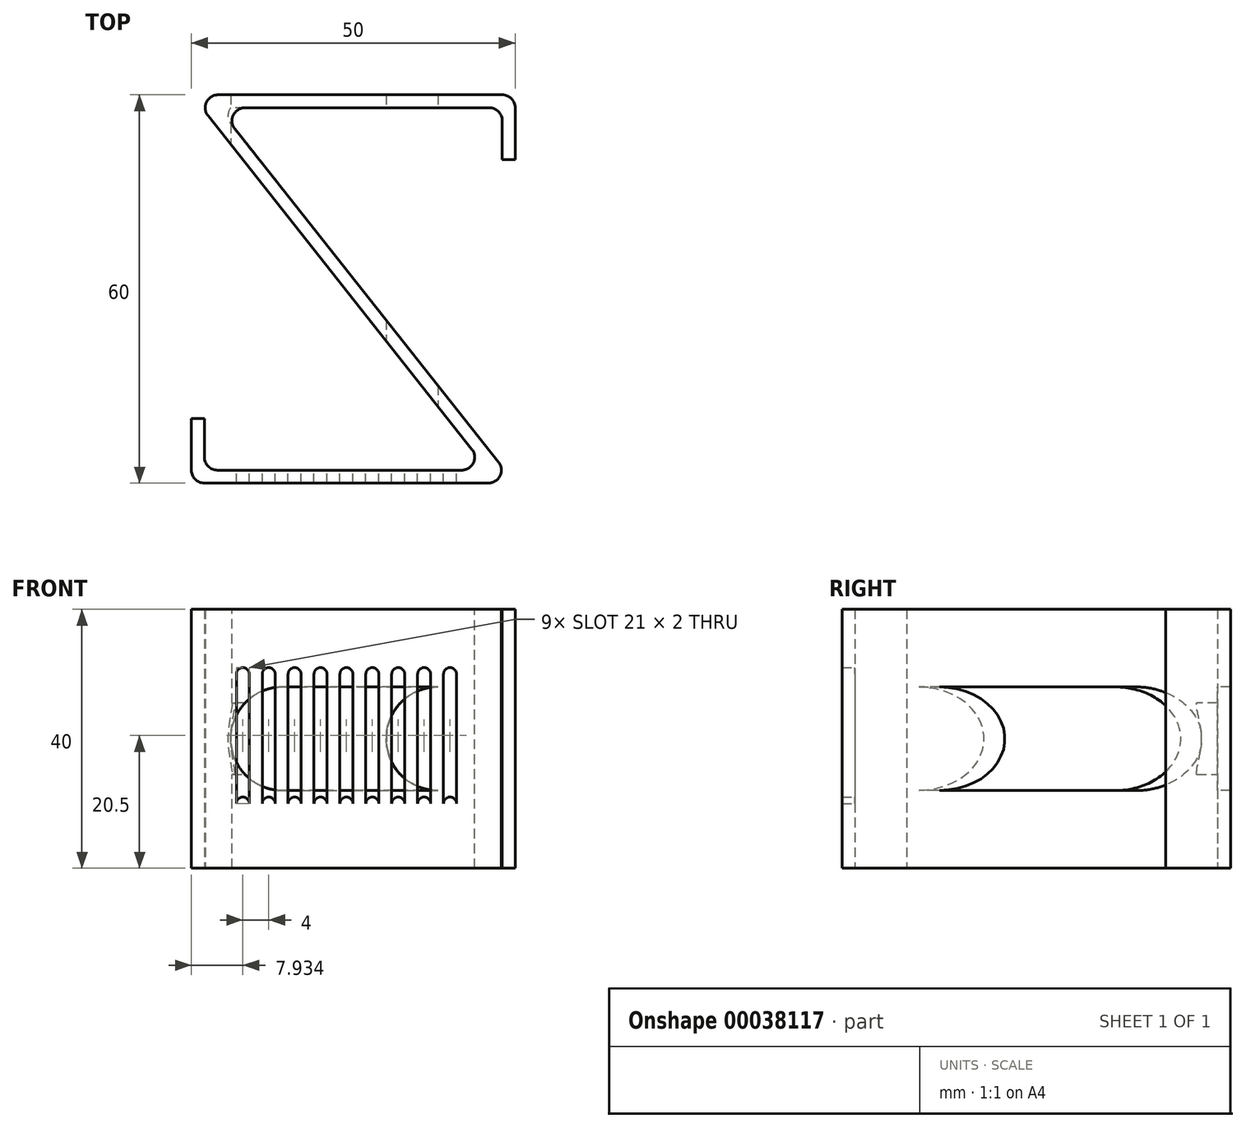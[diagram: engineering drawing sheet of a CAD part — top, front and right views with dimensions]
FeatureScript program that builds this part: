
annotation { "Feature Type Name" : "Feature", "Feature Type Description" : "" }
export const myFeature = defineFeature(function(context is Context, id is Id, definition is map)
    precondition{}
    {
        {
            assignVariable(context, id + "F0", {"name" : "WallThickness", "anyValue" : 2});
        }
        {
            assignVariable(context, id + "F1", {"name" : "Height", "anyValue" : 60});
        }
        {
            var Q0;
            Q0=qCreatedBy(makeId("Top.planeOp"),FACE);
            var sketch = newSketch(context, id + "F2", { "sketchPlane" : qUnion([Q0])});
            skLineSegment(sketch, "E0", {"start": v(0, 10) * mm, "end": v(0, 0) * mm});
            skLineSegment(sketch, "E1", {"start": v(0, 0) * mm, "end": v(50, 0) * mm});
            skLineSegment(sketch, "E2", {"start": v(50, 0) * mm, "end": v(4.13, 58) * mm});
            skLineSegment(sketch, "E3", {"start": v(4.13, 58) * mm, "end": v(48, 58) * mm});
            skLineSegment(sketch, "E4", {"start": v(48, 58) * mm, "end": v(48, 50) * mm});
            skLineSegment(sketch, "E5", {"start": v(48, 50) * mm, "end": v(50, 50) * mm});
            skLineSegment(sketch, "E6", {"start": v(50, 50) * mm, "end": v(50, 60) * mm});
            skLineSegment(sketch, "E7", {"start": v(50, 60) * mm, "end": v(0, 60) * mm});
            skLineSegment(sketch, "E8", {"start": v(0, 60) * mm, "end": v(45.87, 2) * mm});
            skLineSegment(sketch, "E9", {"start": v(45.87, 2) * mm, "end": v(2, 2) * mm});
            skLineSegment(sketch, "E10", {"start": v(2, 2) * mm, "end": v(2, 10) * mm});
            skLineSegment(sketch, "E11", {"start": v(2, 10) * mm, "end": v(0, 10) * mm});
            skSolve(sketch);
        }
        {
            assignVariable(context, id + "F3", {"name" : "Width", "anyValue" : 40});
        }
        {
            var Q0;
            Q0=makeQuery(id+"F2.imprint","IMPRINT",FACE,{"disambiguationData":[TD([[makeQuery(id+"F2.imprint","IMPRINT",EDGE,{"derivedFrom":sQuery(id+"F2.wireOp",EDGE,"E0")}),1.0]])]});
            extrude(context, id + "F4", {"entities" : qUnion([Q0]), "depth" : (getVariable(context, 'Width')) * mm});
        }
        {
            var Q0;
            Q0=makeQuery(id+"F4.opExtrude","SWEPT_FACE",FACE,{"disambiguationData":[OSD([sQuery(id+"F2.wireOp",EDGE,"E3")])]});
            var sketch = newSketch(context, id + "F5", { "sketchPlane" : qUnion([Q0])});
            skLineSegment(sketch, "E12.1", {"start": v(4.13, 40) * mm, "end": v(48, 40) * mm});
            skLineSegment(sketch, "E12.2", {"start": v(48, 40) * mm, "end": v(48, 0) * mm});
            skLineSegment(sketch, "E12.3", {"start": v(4.13, 0) * mm, "end": v(48, 0) * mm});
            skLineSegment(sketch, "E12.4", {"start": v(4.13, 40) * mm, "end": v(4.13, 0) * mm});
            skLineSegment(sketch, "E13", {"start": v(26.07, 40) * mm, "end": v(26.07, 0) * mm, "construction": true});
            skCircle(sketch, "E14", {"center": v(14.07, 20) * mm, "radius": 8 * mm});
            skPoint(sketch, "E14.centerSnap0", {"position": v(26.07, 20) * mm});
            skCircle(sketch, "E15.MirrorC", {"center": v(38.07, 20) * mm, "radius": 8 * mm});
            skLineSegment(sketch, "E16", {"start": v(14.07, 28) * mm, "end": v(38.07, 28) * mm});
            skLineSegment(sketch, "E17", {"start": v(38.07, 12) * mm, "end": v(14.07, 12) * mm});
            skSolve(sketch);
        }
        {
            var Q0;
            {var subQ0=sQuery(id+"F5.wireOp",EDGE,"E14");var subQ2=makeQuery(id+"F5.imprint","INTERSECT",VERTEX,{"derivedFrom":[subQ0,sQuery(id+"F5.wireOp",EDGE,"E16")]});Q0=makeQuery(id+"F5.imprint","IMPRINT",FACE,{"disambiguationData":[TD([[makeQuery(id+"F5.imprint","IMPRINT",EDGE,{"disambiguationData":[TD([[subQ2,-1.0]])],"derivedFrom":subQ0}),1.0]])]});}
            var Q1;
            {var subQ1=sQuery(id+"F5.wireOp",EDGE,"E16");Q1=makeQuery(id+"F5.imprint","IMPRINT",FACE,{"disambiguationData":[TD([[makeQuery(id+"F5.imprint","IMPRINT",EDGE,{"derivedFrom":subQ1}),-1.0]])]});}
            var Q2;
            {var subQ0=sQuery(id+"F5.wireOp",EDGE,"E15.MirrorC");var subQ2=makeQuery(id+"F5.imprint","INTERSECT",VERTEX,{"derivedFrom":[subQ0,sQuery(id+"F5.wireOp",EDGE,"E16")]});Q2=makeQuery(id+"F5.imprint","IMPRINT",FACE,{"disambiguationData":[TD([[makeQuery(id+"F5.imprint","IMPRINT",EDGE,{"disambiguationData":[TD([[subQ2,-1.0]])],"derivedFrom":subQ0}),-1.0]])]});}
            extrude(context, id + "F6", {"entities" : qUnion([Q0, Q1, Q2]), "operationType" : NewBodyOperationType.REMOVE, "endBound" : BoundingType.THROUGH_ALL, "oppositeDirection" : true, "depth" : 25 * mm, "hasSecondDirection" : true, "secondDirectionOppositeDirection" : false, "secondDirectionDepth" : (getVariable(context, 'Height') - (getVariable(context, 'WallThickness') * 2)) * mm});
        }
        {
            var Q0;
            Q0=makeQuery(id+"F4.opExtrude","SWEPT_FACE",FACE,{"disambiguationData":[OSD([sQuery(id+"F2.wireOp",EDGE,"E9")])]});
            var sketch = newSketch(context, id + "F7", { "sketchPlane" : qUnion([Q0])});
            skLineSegment(sketch, "E18.0", {"start": v(-45.87, 0) * mm, "end": v(-2, 0) * mm});
            skLineSegment(sketch, "E18.1", {"start": v(-2, 40) * mm, "end": v(-2, 0) * mm});
            skLineSegment(sketch, "E18.2", {"start": v(-45.87, 40) * mm, "end": v(-2, 40) * mm});
            skLineSegment(sketch, "E18.3", {"start": v(-45.87, 40) * mm, "end": v(-45.87, 0) * mm});
            skLineSegment(sketch, "E19", {"start": v(-23.93, 40) * mm, "end": v(-23.93, 0) * mm, "construction": true});
            skCircle(sketch, "E20", {"center": v(-23.93, 30) * mm, "radius": 1 * mm});
            skLineSegment(sketch, "E21", {"start": v(-45.87, 20) * mm, "end": v(-2, 20) * mm, "construction": true});
            skCircle(sketch, "E22.MirrorC", {"center": v(-23.93, 10) * mm, "radius": 1 * mm});
            skLineSegment(sketch, "E23", {"start": v(-22.93, 10) * mm, "end": v(-22.93, 30) * mm});
            skLineSegment(sketch, "E24", {"start": v(-24.93, 30) * mm, "end": v(-24.93, 10) * mm});
            skCircle(sketch, "E25.1.0.0", {"center": v(-19.93, 10) * mm, "radius": 1 * mm});
            skCircle(sketch, "E25.1.0.1", {"center": v(-19.93, 30) * mm, "radius": 1 * mm});
            skLineSegment(sketch, "E25.1.0.2", {"start": v(-20.93, 30) * mm, "end": v(-20.93, 10) * mm});
            skLineSegment(sketch, "E25.1.0.3", {"start": v(-18.93, 10) * mm, "end": v(-18.93, 30) * mm});
            skCircle(sketch, "E25.2.0.0", {"center": v(-15.93, 10) * mm, "radius": 1 * mm});
            skCircle(sketch, "E25.2.0.1", {"center": v(-15.93, 30) * mm, "radius": 1 * mm});
            skLineSegment(sketch, "E25.2.0.2", {"start": v(-16.93, 30) * mm, "end": v(-16.93, 10) * mm});
            skLineSegment(sketch, "E25.2.0.3", {"start": v(-14.93, 10) * mm, "end": v(-14.93, 30) * mm});
            skCircle(sketch, "E25.3.0.0", {"center": v(-11.93, 10) * mm, "radius": 1 * mm});
            skCircle(sketch, "E25.3.0.1", {"center": v(-11.93, 30) * mm, "radius": 1 * mm});
            skLineSegment(sketch, "E25.3.0.2", {"start": v(-12.93, 30) * mm, "end": v(-12.93, 10) * mm});
            skLineSegment(sketch, "E25.3.0.3", {"start": v(-10.93, 10) * mm, "end": v(-10.93, 30) * mm});
            skCircle(sketch, "E25.4.0.0", {"center": v(-7.93, 10) * mm, "radius": 1 * mm});
            skCircle(sketch, "E25.4.0.1", {"center": v(-7.93, 30) * mm, "radius": 1 * mm});
            skLineSegment(sketch, "E25.4.0.2", {"start": v(-8.93, 30) * mm, "end": v(-8.93, 10) * mm});
            skLineSegment(sketch, "E25.4.0.3", {"start": v(-6.93, 10) * mm, "end": v(-6.93, 30) * mm});
            skLineSegment(sketch, "E25.direction1", {"start": v(-23.93, 10) * mm, "end": v(-19.93, 10) * mm, "construction": true});
            skLineSegment(sketch, "E26.1.0.0", {"start": v(-28.93, 30) * mm, "end": v(-28.93, 10) * mm});
            skLineSegment(sketch, "E26.1.0.1", {"start": v(-26.93, 10) * mm, "end": v(-26.93, 30) * mm});
            skCircle(sketch, "E26.1.0.2", {"center": v(-27.93, 10) * mm, "radius": 1 * mm});
            skCircle(sketch, "E26.1.0.3", {"center": v(-27.93, 30) * mm, "radius": 1 * mm});
            skLineSegment(sketch, "E26.2.0.0", {"start": v(-32.93, 30) * mm, "end": v(-32.93, 10) * mm});
            skLineSegment(sketch, "E26.2.0.1", {"start": v(-30.93, 10) * mm, "end": v(-30.93, 30) * mm});
            skCircle(sketch, "E26.2.0.2", {"center": v(-31.93, 10) * mm, "radius": 1 * mm});
            skCircle(sketch, "E26.2.0.3", {"center": v(-31.93, 30) * mm, "radius": 1 * mm});
            skLineSegment(sketch, "E26.3.0.0", {"start": v(-36.93, 30) * mm, "end": v(-36.93, 10) * mm});
            skLineSegment(sketch, "E26.3.0.1", {"start": v(-34.93, 10) * mm, "end": v(-34.93, 30) * mm});
            skCircle(sketch, "E26.3.0.2", {"center": v(-35.93, 10) * mm, "radius": 1 * mm});
            skCircle(sketch, "E26.3.0.3", {"center": v(-35.93, 30) * mm, "radius": 1 * mm});
            skLineSegment(sketch, "E26.4.0.0", {"start": v(-40.93, 30) * mm, "end": v(-40.93, 10) * mm});
            skLineSegment(sketch, "E26.4.0.1", {"start": v(-38.93, 10) * mm, "end": v(-38.93, 30) * mm});
            skCircle(sketch, "E26.4.0.2", {"center": v(-39.93, 10) * mm, "radius": 1 * mm});
            skCircle(sketch, "E26.4.0.3", {"center": v(-39.93, 30) * mm, "radius": 1 * mm});
            skLineSegment(sketch, "E26.direction1", {"start": v(-24.93, 10) * mm, "end": v(-28.93, 10) * mm, "construction": true});
            skSolve(sketch);
        }
        {
            var Q0;
            {var subQ0=sQuery(id+"F7.wireOp",EDGE,"E25.4.0.0");var subQ2=makeQuery(id+"F7.imprint","INTERSECT",VERTEX,{"derivedFrom":[subQ0,sQuery(id+"F7.wireOp",EDGE,"E25.4.0.2")]});Q0=makeQuery(id+"F7.imprint","IMPRINT",FACE,{"disambiguationData":[TD([[makeQuery(id+"F7.imprint","IMPRINT",EDGE,{"disambiguationData":[TD([[subQ2,1.0]])],"derivedFrom":subQ0}),-1.0]])]});}
            var Q1;
            {var subQ2=sQuery(id+"F7.wireOp",EDGE,"E25.4.0.2");Q1=makeQuery(id+"F7.imprint","IMPRINT",FACE,{"disambiguationData":[TD([[makeQuery(id+"F7.imprint","IMPRINT",EDGE,{"derivedFrom":subQ2}),1.0]])]});}
            var Q2;
            {var subQ0=sQuery(id+"F7.wireOp",EDGE,"E25.4.0.1");var subQ2=makeQuery(id+"F7.imprint","INTERSECT",VERTEX,{"derivedFrom":[subQ0,sQuery(id+"F7.wireOp",EDGE,"E25.4.0.2")]});Q2=makeQuery(id+"F7.imprint","IMPRINT",FACE,{"disambiguationData":[TD([[makeQuery(id+"F7.imprint","IMPRINT",EDGE,{"disambiguationData":[TD([[subQ2,1.0]])],"derivedFrom":subQ0}),1.0]])]});}
            var Q3;
            {var subQ0=sQuery(id+"F7.wireOp",EDGE,"E25.3.0.0");var subQ2=makeQuery(id+"F7.imprint","INTERSECT",VERTEX,{"derivedFrom":[subQ0,sQuery(id+"F7.wireOp",EDGE,"E25.3.0.2")]});Q3=makeQuery(id+"F7.imprint","IMPRINT",FACE,{"disambiguationData":[TD([[makeQuery(id+"F7.imprint","IMPRINT",EDGE,{"disambiguationData":[TD([[subQ2,1.0]])],"derivedFrom":subQ0}),-1.0]])]});}
            var Q4;
            {var subQ0=sQuery(id+"F7.wireOp",EDGE,"E25.3.0.2");Q4=makeQuery(id+"F7.imprint","IMPRINT",FACE,{"disambiguationData":[TD([[makeQuery(id+"F7.imprint","IMPRINT",EDGE,{"derivedFrom":subQ0}),1.0]])]});}
            var Q5;
            {var subQ0=sQuery(id+"F7.wireOp",EDGE,"E25.3.0.1");var subQ2=makeQuery(id+"F7.imprint","INTERSECT",VERTEX,{"derivedFrom":[subQ0,sQuery(id+"F7.wireOp",EDGE,"E25.3.0.2")]});Q5=makeQuery(id+"F7.imprint","IMPRINT",FACE,{"disambiguationData":[TD([[makeQuery(id+"F7.imprint","IMPRINT",EDGE,{"disambiguationData":[TD([[subQ2,1.0]])],"derivedFrom":subQ0}),1.0]])]});}
            var Q6;
            {var subQ0=sQuery(id+"F7.wireOp",EDGE,"E25.2.0.1");var subQ2=makeQuery(id+"F7.imprint","INTERSECT",VERTEX,{"derivedFrom":[subQ0,sQuery(id+"F7.wireOp",EDGE,"E25.2.0.2")]});Q6=makeQuery(id+"F7.imprint","IMPRINT",FACE,{"disambiguationData":[TD([[makeQuery(id+"F7.imprint","IMPRINT",EDGE,{"disambiguationData":[TD([[subQ2,1.0]])],"derivedFrom":subQ0}),1.0]])]});}
            var Q7;
            {var subQ0=sQuery(id+"F7.wireOp",EDGE,"E25.2.0.2");Q7=makeQuery(id+"F7.imprint","IMPRINT",FACE,{"disambiguationData":[TD([[makeQuery(id+"F7.imprint","IMPRINT",EDGE,{"derivedFrom":subQ0}),1.0]])]});}
            var Q8;
            {var subQ0=sQuery(id+"F7.wireOp",EDGE,"E25.2.0.0");var subQ2=makeQuery(id+"F7.imprint","INTERSECT",VERTEX,{"derivedFrom":[subQ0,sQuery(id+"F7.wireOp",EDGE,"E25.2.0.2")]});Q8=makeQuery(id+"F7.imprint","IMPRINT",FACE,{"disambiguationData":[TD([[makeQuery(id+"F7.imprint","IMPRINT",EDGE,{"disambiguationData":[TD([[subQ2,1.0]])],"derivedFrom":subQ0}),-1.0]])]});}
            var Q9;
            {var subQ0=sQuery(id+"F7.wireOp",EDGE,"E25.1.0.0");var subQ2=makeQuery(id+"F7.imprint","INTERSECT",VERTEX,{"derivedFrom":[subQ0,sQuery(id+"F7.wireOp",EDGE,"E25.1.0.2")]});Q9=makeQuery(id+"F7.imprint","IMPRINT",FACE,{"disambiguationData":[TD([[makeQuery(id+"F7.imprint","IMPRINT",EDGE,{"disambiguationData":[TD([[subQ2,1.0]])],"derivedFrom":subQ0}),-1.0]])]});}
            var Q10;
            {var subQ0=sQuery(id+"F7.wireOp",EDGE,"E25.1.0.2");Q10=makeQuery(id+"F7.imprint","IMPRINT",FACE,{"disambiguationData":[TD([[makeQuery(id+"F7.imprint","IMPRINT",EDGE,{"derivedFrom":subQ0}),1.0]])]});}
            var Q11;
            {var subQ0=sQuery(id+"F7.wireOp",EDGE,"E25.1.0.1");var subQ2=makeQuery(id+"F7.imprint","INTERSECT",VERTEX,{"derivedFrom":[subQ0,sQuery(id+"F7.wireOp",EDGE,"E25.1.0.2")]});Q11=makeQuery(id+"F7.imprint","IMPRINT",FACE,{"disambiguationData":[TD([[makeQuery(id+"F7.imprint","IMPRINT",EDGE,{"disambiguationData":[TD([[subQ2,1.0]])],"derivedFrom":subQ0}),1.0]])]});}
            var Q12;
            {var subQ0=sQuery(id+"F7.wireOp",EDGE,"E20");var subQ2=makeQuery(id+"F7.imprint","INTERSECT",VERTEX,{"derivedFrom":[subQ0,sQuery(id+"F7.wireOp",EDGE,"E23")]});Q12=makeQuery(id+"F7.imprint","IMPRINT",FACE,{"disambiguationData":[TD([[makeQuery(id+"F7.imprint","IMPRINT",EDGE,{"disambiguationData":[TD([[subQ2,-1.0]])],"derivedFrom":subQ0}),1.0]])]});}
            var Q13;
            {var subQ1=sQuery(id+"F7.wireOp",EDGE,"E23");Q13=makeQuery(id+"F7.imprint","IMPRINT",FACE,{"disambiguationData":[TD([[makeQuery(id+"F7.imprint","IMPRINT",EDGE,{"derivedFrom":subQ1}),1.0]])]});}
            var Q14;
            {var subQ0=sQuery(id+"F7.wireOp",EDGE,"E22.MirrorC");var subQ2=makeQuery(id+"F7.imprint","INTERSECT",VERTEX,{"derivedFrom":[subQ0,sQuery(id+"F7.wireOp",EDGE,"E23")]});Q14=makeQuery(id+"F7.imprint","IMPRINT",FACE,{"disambiguationData":[TD([[makeQuery(id+"F7.imprint","IMPRINT",EDGE,{"disambiguationData":[TD([[subQ2,-1.0]])],"derivedFrom":subQ0}),-1.0]])]});}
            var Q15;
            {var subQ0=sQuery(id+"F7.wireOp",EDGE,"E26.1.0.2");var subQ2=makeQuery(id+"F7.imprint","INTERSECT",VERTEX,{"derivedFrom":[sQuery(id+"F7.wireOp",EDGE,"E26.1.0.0"),subQ0]});Q15=makeQuery(id+"F7.imprint","IMPRINT",FACE,{"disambiguationData":[TD([[makeQuery(id+"F7.imprint","IMPRINT",EDGE,{"disambiguationData":[TD([[subQ2,1.0]])],"derivedFrom":subQ0}),-1.0]])]});}
            var Q16;
            {var subQ2=sQuery(id+"F7.wireOp",EDGE,"E26.1.0.0");Q16=makeQuery(id+"F7.imprint","IMPRINT",FACE,{"disambiguationData":[TD([[makeQuery(id+"F7.imprint","IMPRINT",EDGE,{"derivedFrom":subQ2}),1.0]])]});}
            var Q17;
            {var subQ0=sQuery(id+"F7.wireOp",EDGE,"E26.1.0.3");var subQ2=makeQuery(id+"F7.imprint","INTERSECT",VERTEX,{"derivedFrom":[sQuery(id+"F7.wireOp",EDGE,"E26.1.0.0"),subQ0]});Q17=makeQuery(id+"F7.imprint","IMPRINT",FACE,{"disambiguationData":[TD([[makeQuery(id+"F7.imprint","IMPRINT",EDGE,{"disambiguationData":[TD([[subQ2,1.0]])],"derivedFrom":subQ0}),1.0]])]});}
            var Q18;
            {var subQ0=sQuery(id+"F7.wireOp",EDGE,"E26.2.0.3");var subQ2=makeQuery(id+"F7.imprint","INTERSECT",VERTEX,{"derivedFrom":[sQuery(id+"F7.wireOp",EDGE,"E26.2.0.0"),subQ0]});Q18=makeQuery(id+"F7.imprint","IMPRINT",FACE,{"disambiguationData":[TD([[makeQuery(id+"F7.imprint","IMPRINT",EDGE,{"disambiguationData":[TD([[subQ2,1.0]])],"derivedFrom":subQ0}),1.0]])]});}
            var Q19;
            {var subQ2=sQuery(id+"F7.wireOp",EDGE,"E26.2.0.0");Q19=makeQuery(id+"F7.imprint","IMPRINT",FACE,{"disambiguationData":[TD([[makeQuery(id+"F7.imprint","IMPRINT",EDGE,{"derivedFrom":subQ2}),1.0]])]});}
            var Q20;
            {var subQ0=sQuery(id+"F7.wireOp",EDGE,"E26.2.0.2");var subQ2=makeQuery(id+"F7.imprint","INTERSECT",VERTEX,{"derivedFrom":[sQuery(id+"F7.wireOp",EDGE,"E26.2.0.0"),subQ0]});Q20=makeQuery(id+"F7.imprint","IMPRINT",FACE,{"disambiguationData":[TD([[makeQuery(id+"F7.imprint","IMPRINT",EDGE,{"disambiguationData":[TD([[subQ2,1.0]])],"derivedFrom":subQ0}),-1.0]])]});}
            var Q21;
            {var subQ0=sQuery(id+"F7.wireOp",EDGE,"E26.3.0.2");var subQ2=makeQuery(id+"F7.imprint","INTERSECT",VERTEX,{"derivedFrom":[sQuery(id+"F7.wireOp",EDGE,"E26.3.0.0"),subQ0]});Q21=makeQuery(id+"F7.imprint","IMPRINT",FACE,{"disambiguationData":[TD([[makeQuery(id+"F7.imprint","IMPRINT",EDGE,{"disambiguationData":[TD([[subQ2,1.0]])],"derivedFrom":subQ0}),-1.0]])]});}
            var Q22;
            {var subQ2=sQuery(id+"F7.wireOp",EDGE,"E26.3.0.0");Q22=makeQuery(id+"F7.imprint","IMPRINT",FACE,{"disambiguationData":[TD([[makeQuery(id+"F7.imprint","IMPRINT",EDGE,{"derivedFrom":subQ2}),1.0]])]});}
            var Q23;
            {var subQ0=sQuery(id+"F7.wireOp",EDGE,"E26.3.0.3");var subQ2=makeQuery(id+"F7.imprint","INTERSECT",VERTEX,{"derivedFrom":[sQuery(id+"F7.wireOp",EDGE,"E26.3.0.0"),subQ0]});Q23=makeQuery(id+"F7.imprint","IMPRINT",FACE,{"disambiguationData":[TD([[makeQuery(id+"F7.imprint","IMPRINT",EDGE,{"disambiguationData":[TD([[subQ2,1.0]])],"derivedFrom":subQ0}),1.0]])]});}
            var Q24;
            {var subQ0=sQuery(id+"F7.wireOp",EDGE,"E26.4.0.2");var subQ2=makeQuery(id+"F7.imprint","INTERSECT",VERTEX,{"derivedFrom":[sQuery(id+"F7.wireOp",EDGE,"E26.4.0.0"),subQ0]});Q24=makeQuery(id+"F7.imprint","IMPRINT",FACE,{"disambiguationData":[TD([[makeQuery(id+"F7.imprint","IMPRINT",EDGE,{"disambiguationData":[TD([[subQ2,1.0]])],"derivedFrom":subQ0}),-1.0]])]});}
            var Q25;
            {var subQ2=sQuery(id+"F7.wireOp",EDGE,"E26.4.0.0");Q25=makeQuery(id+"F7.imprint","IMPRINT",FACE,{"disambiguationData":[TD([[makeQuery(id+"F7.imprint","IMPRINT",EDGE,{"derivedFrom":subQ2}),1.0]])]});}
            var Q26;
            {var subQ0=sQuery(id+"F7.wireOp",EDGE,"E26.4.0.3");var subQ2=makeQuery(id+"F7.imprint","INTERSECT",VERTEX,{"derivedFrom":[sQuery(id+"F7.wireOp",EDGE,"E26.4.0.0"),subQ0]});Q26=makeQuery(id+"F7.imprint","IMPRINT",FACE,{"disambiguationData":[TD([[makeQuery(id+"F7.imprint","IMPRINT",EDGE,{"disambiguationData":[TD([[subQ2,1.0]])],"derivedFrom":subQ0}),1.0]])]});}
            extrude(context, id + "F8", {"entities" : qUnion([Q0, Q1, Q2, Q3, Q4, Q5, Q6, Q7, Q8, Q9, Q10, Q11, Q12, Q13, Q14, Q15, Q16, Q17, Q18, Q19, Q20, Q21, Q22, Q23, Q24, Q25, Q26]), "operationType" : NewBodyOperationType.REMOVE, "endBound" : BoundingType.THROUGH_ALL, "oppositeDirection" : true, "depth" : 25 * mm});
        }
        {
            var Q0;
            Q0=makeQuery(id+"F4.opExtrude","SWEPT_EDGE",EDGE,{"disambiguationData":[OSD([sQuery(id+"F2.wireOp",EDGE,"E0"),sQuery(id+"F2.wireOp",EDGE,"E1")])]});
            var Q1;
            Q1=makeQuery(id+"F4.opExtrude","SWEPT_EDGE",EDGE,{"disambiguationData":[OSD([sQuery(id+"F2.wireOp",EDGE,"E9"),sQuery(id+"F2.wireOp",EDGE,"E10")])]});
            var Q2;
            Q2=makeQuery(id+"F4.opExtrude","SWEPT_EDGE",EDGE,{"disambiguationData":[OSD([sQuery(id+"F2.wireOp",EDGE,"E1"),sQuery(id+"F2.wireOp",EDGE,"E2")])]});
            var Q3;
            Q3=makeQuery(id+"F4.opExtrude","SWEPT_EDGE",EDGE,{"disambiguationData":[OSD([sQuery(id+"F2.wireOp",EDGE,"E8"),sQuery(id+"F2.wireOp",EDGE,"E9")])]});
            var Q4;
            Q4=makeQuery(id+"F4.opExtrude","SWEPT_EDGE",EDGE,{"disambiguationData":[OSD([sQuery(id+"F2.wireOp",EDGE,"E2"),sQuery(id+"F2.wireOp",EDGE,"E3")])]});
            var Q5;
            Q5=makeQuery(id+"F4.opExtrude","SWEPT_EDGE",EDGE,{"disambiguationData":[OSD([sQuery(id+"F2.wireOp",EDGE,"E6"),sQuery(id+"F2.wireOp",EDGE,"E7")])]});
            var Q6;
            Q6=makeQuery(id+"F4.opExtrude","SWEPT_EDGE",EDGE,{"disambiguationData":[OSD([sQuery(id+"F2.wireOp",EDGE,"E3"),sQuery(id+"F2.wireOp",EDGE,"E4")])]});
            var Q7;
            Q7=makeQuery(id+"F4.opExtrude","SWEPT_EDGE",EDGE,{"disambiguationData":[OSD([sQuery(id+"F2.wireOp",EDGE,"E7"),sQuery(id+"F2.wireOp",EDGE,"E8")])]});
            fillet(context, id + "F9", {"entities" : qUnion([Q0, Q1, Q2, Q3, Q4, Q5, Q6, Q7]), "radius" : (getVariable(context, 'WallThickness')) * mm, "tangentPropagation" : true, "allowEdgeOverflow" : false});
        }
    });
